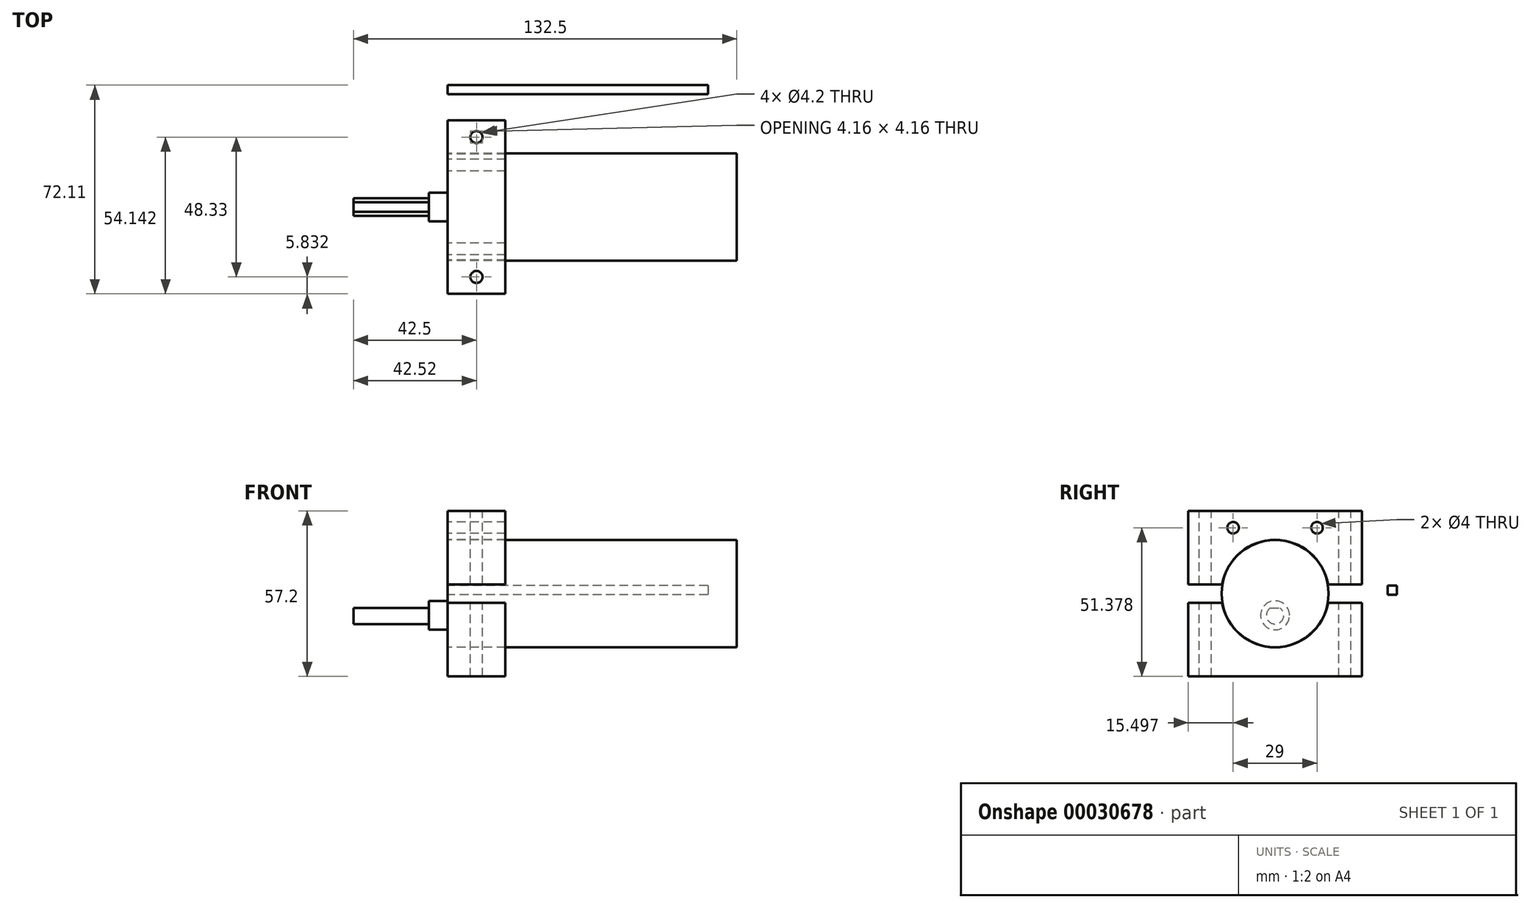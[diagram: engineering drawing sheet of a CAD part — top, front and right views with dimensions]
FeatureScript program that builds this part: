
annotation { "Feature Type Name" : "Feature", "Feature Type Description" : "" }
export const myFeature = defineFeature(function(context is Context, id is Id, definition is map)
    precondition{}
    {
        {
            var Q0;
            Q0=qCreatedBy(makeId("Right.planeOp"),FACE);
            var sketch = newSketch(context, id + "F0", { "sketchPlane" : qUnion([Q0])});
            skLineSegment(sketch, "E0", {"start": v(-30.1, 27.66) * mm, "end": v(29.9, 27.66) * mm});
            skLineSegment(sketch, "E1", {"start": v(-30.1, 27.66) * mm, "end": v(-30.1, 2.22) * mm});
            skLineSegment(sketch, "E2", {"start": v(29.9, 27.66) * mm, "end": v(29.9, 2.22) * mm});
            skPoint(sketch, "E3", {"position": v(-0.1, -0.94) * mm});
            skArc(sketch, "E4", {"start": v(18.23, 2.22) * mm, "mid": v(-0.1, 17.66) * mm, "end": v(-18.43, 2.22) * mm});
            skPoint(sketch, "E5", {"position": v(-0.1, 17.66) * mm});
            skLineSegment(sketch, "E6.trimOffspring", {"start": v(18.23, 2.22) * mm, "end": v(29.9, 2.22) * mm});
            skPoint(sketch, "E7.start.orphan", {"position": v(-0.1, 27.66) * mm});
            skLineSegment(sketch, "E8", {"start": v(-30.1, 2.22) * mm, "end": v(-18.43, 2.22) * mm});
            skCircle(sketch, "E9", {"center": v(-0.1, -0.94) * mm, "radius": 18.5 * mm});
            skLineSegment(sketch, "E10", {"start": v(-30.1, -0.94) * mm, "end": v(34.22, -0.94) * mm});
            skLineSegment(sketch, "E11.MirrorCS", {"start": v(29.9, -29.54) * mm, "end": v(29.9, -4.1) * mm});
            skLineSegment(sketch, "E12.MirrorCS", {"start": v(18.23, -4.1) * mm, "end": v(29.9, -4.1) * mm});
            skLineSegment(sketch, "E13.MirrorCS", {"start": v(-30.1, -29.54) * mm, "end": v(29.9, -29.54) * mm});
            skLineSegment(sketch, "E14.MirrorCS", {"start": v(-30.1, -29.54) * mm, "end": v(-30.1, -4.1) * mm});
            skLineSegment(sketch, "E15.MirrorCS", {"start": v(-30.1, -4.1) * mm, "end": v(-18.43, -4.1) * mm});
            skArc(sketch, "E16.MirrorCS", {"start": v(18.23, -4.1) * mm, "mid": v(-0.1, -19.54) * mm, "end": v(-18.43, -4.1) * mm});
            skCircle(sketch, "E17", {"center": v(-0.1, -0.94) * mm, "radius": 12.5 * mm});
            skPoint(sketch, "E18", {"position": v(-0.1, -8.44) * mm});
            skPoint(sketch, "E19.end.orphan", {"position": v(-0.1, -13.44) * mm});
            skCircle(sketch, "E20", {"center": v(-0.1, -8.44) * mm, "radius": 5 * mm});
            skSolve(sketch);
        }
        {
            var Q0;
            Q0=makeQuery(id+"F0.imprint","IMPRINT",FACE,{"disambiguationData":[TD([[makeQuery(id+"F0.imprint","IMPRINT",EDGE,{"derivedFrom":sQuery(id+"F0.wireOp",EDGE,"E0")}),-1.0]])]});
            var Q1;
            Q1=makeQuery(id+"F0.imprint","IMPRINT",FACE,{"disambiguationData":[TD([[makeQuery(id+"F0.imprint","IMPRINT",EDGE,{"derivedFrom":sQuery(id+"F0.wireOp",EDGE,"E11.MirrorCS")}),1.0]])]});
            extrude(context, id + "F1", {"entities" : qUnion([Q0, Q1]), "depth" : 20 * mm});
        }
        {
            var Q0;
            Q0=makeQuery(id+"F1.opExtrude","SWEPT_FACE",FACE,{"disambiguationData":[OSD([sQuery(id+"F0.wireOp",EDGE,"E0")])]});
            var sketch = newSketch(context, id + "F2", { "sketchPlane" : qUnion([Q0])});
            skPoint(sketch, "E21.0", {"position": v(0, -30.1) * mm});
            skPoint(sketch, "E22.0", {"position": v(20, -30.1) * mm});
            skPoint(sketch, "E23.0", {"position": v(0, 29.9) * mm});
            skPoint(sketch, "E24.0", {"position": v(20, 29.9) * mm});
            skLineSegment(sketch, "E25.0.0", {"start": v(0, 29.9) * mm, "end": v(0, -30.1) * mm});
            skLineSegment(sketch, "E25.0.1", {"start": v(0, -30.1) * mm, "end": v(20, -30.1) * mm});
            skLineSegment(sketch, "E25.0.2", {"start": v(20, -30.1) * mm, "end": v(20, 29.9) * mm});
            skLineSegment(sketch, "E25.0.3", {"start": v(20, 29.9) * mm, "end": v(0, 29.9) * mm});
            skPoint(sketch, "E26.0", {"position": v(0, -18.43) * mm});
            skPoint(sketch, "E27.0", {"position": v(20, -18.43) * mm});
            skPoint(sketch, "E28.0", {"position": v(20, 18.23) * mm});
            skPoint(sketch, "E29.0", {"position": v(0, 18.23) * mm});
            skCircle(sketch, "E30", {"center": v(10, 24.06) * mm, "radius": 2.1 * mm});
            skCircle(sketch, "E31", {"center": v(10, -24.27) * mm, "radius": 2.1 * mm});
            skSolve(sketch);
        }
        {
            var Q0;
            Q0=makeQuery(id+"F2.imprint","IMPRINT",FACE,{"disambiguationData":[TD([[makeQuery(id+"F2.imprint","IMPRINT",EDGE,{"derivedFrom":sQuery(id+"F2.wireOp",EDGE,"E31")}),1.0]])]});
            var Q1;
            Q1=makeQuery(id+"F2.imprint","IMPRINT",FACE,{"disambiguationData":[TD([[makeQuery(id+"F2.imprint","IMPRINT",EDGE,{"derivedFrom":sQuery(id+"F2.wireOp",EDGE,"E30")}),1.0]])]});
            var Q2;
            Q2=makeQuery(id+"F1.opExtrude","SWEPT_FACE",FACE,{"disambiguationData":[OSD([sQuery(id+"F0.wireOp",EDGE,"E13.MirrorCS")])]});
            extrude(context, id + "F3", {"entities" : qUnion([Q0, Q1]), "operationType" : NewBodyOperationType.REMOVE, "endBound" : BoundingType.UP_TO_SURFACE, "oppositeDirection" : true, "endBoundEntityFace" : qUnion([Q2]), "depth" : 25 * mm});
        }
        {
            var Q0;
            Q0=qCreatedBy(makeId("Right.planeOp"),FACE);
            var sketch = newSketch(context, id + "F4", { "sketchPlane" : qUnion([Q0])});
            skLineSegment(sketch, "E32.bottom", {"start": v(42.01, 1.83) * mm, "end": v(38.84, 1.83) * mm});
            skLineSegment(sketch, "E32.top", {"start": v(42.01, -1.34) * mm, "end": v(38.84, -1.34) * mm});
            skLineSegment(sketch, "E32.left", {"start": v(42.01, 1.83) * mm, "end": v(42.01, -1.34) * mm});
            skLineSegment(sketch, "E32.right", {"start": v(38.84, 1.83) * mm, "end": v(38.84, -1.34) * mm});
            skPoint(sketch, "E33", {"position": v(40.43, 0.25) * mm});
            skSolve(sketch);
        }
        {
            var Q0;
            Q0=makeQuery(id+"F4.imprint","IMPRINT",FACE,{"disambiguationData":[TD([[makeQuery(id+"F4.imprint","IMPRINT",EDGE,{"derivedFrom":sQuery(id+"F4.wireOp",EDGE,"E32.bottom")}),1.0]])]});
            extrude(context, id + "F5", {"entities" : qUnion([Q0]), "depth" : 90 * mm});
        }
        {
            var Q0;
            {var subQ2=sQuery(id+"F0.wireOp",EDGE,"E10");var subQ4=sQuery(id+"F0.wireOp",EDGE,"E9");var subQ5=makeQuery(id+"F0.imprint","INTERSECT",VERTEX,{"disambiguationData":[OD(0.0)],"derivedFrom":[subQ4,subQ2]});Q0=makeQuery(id+"F0.imprint","IMPRINT",FACE,{"disambiguationData":[TD([[makeQuery(id+"F0.imprint","IMPRINT",EDGE,{"disambiguationData":[TD([[subQ5,-1.0]])],"derivedFrom":subQ4}),1.0]])]});}
            var Q1;
            {var subQ4=sQuery(id+"F0.wireOp",EDGE,"E20");Q1=makeQuery(id+"F0.imprint","IMPRINT",FACE,{"disambiguationData":[TD([[makeQuery(id+"F0.imprint","IMPRINT",EDGE,{"derivedFrom":subQ4}),-1.0]])]});}
            var Q2;
            {var subQ0=sQuery(id+"F0.wireOp",EDGE,"E10");var subQ1=sQuery(id+"F0.wireOp",EDGE,"E9");var subQ2=makeQuery(id+"F0.imprint","INTERSECT",VERTEX,{"disambiguationData":[OD(0.0)],"derivedFrom":[subQ1,subQ0]});Q2=makeQuery(id+"F0.imprint","IMPRINT",FACE,{"disambiguationData":[TD([[makeQuery(id+"F0.imprint","IMPRINT",EDGE,{"disambiguationData":[TD([[subQ2,1.0]])],"derivedFrom":subQ1}),1.0]])]});}
            var Q3;
            {var subQ0=sQuery(id+"F0.wireOp",EDGE,"E17");var subQ1=sQuery(id+"F0.wireOp",EDGE,"E10");var subQ2=makeQuery(id+"F0.imprint","INTERSECT",VERTEX,{"disambiguationData":[OD(0.0)],"derivedFrom":[subQ1,subQ0]});Q3=makeQuery(id+"F0.imprint","IMPRINT",FACE,{"disambiguationData":[TD([[makeQuery(id+"F0.imprint","IMPRINT",EDGE,{"disambiguationData":[TD([[subQ2,-1.0]])],"derivedFrom":subQ1}),1.0]])]});}
            var Q4;
            Q4=makeQuery(id+"F0.imprint","IMPRINT",FACE,{"disambiguationData":[TD([[makeQuery(id+"F0.imprint","IMPRINT",EDGE,{"derivedFrom":sQuery(id+"F0.wireOp",EDGE,"E20")}),1.0]])]});
            extrude(context, id + "F6", {"entities" : qUnion([Q0, Q1, Q2, Q3, Q4]), "depth" : 100 * mm});
        }
        {
            var Q0;
            Q0=makeQuery(id+"F0.imprint","IMPRINT",FACE,{"disambiguationData":[TD([[makeQuery(id+"F0.imprint","IMPRINT",EDGE,{"derivedFrom":sQuery(id+"F0.wireOp",EDGE,"E20")}),1.0]])]});
            extrude(context, id + "F7", {"entities" : qUnion([Q0]), "operationType" : NewBodyOperationType.ADD, "oppositeDirection" : true, "depth" : 6.5 * mm});
        }
        {
            var Q0;
            Q0=qCreatedBy(makeId("Right.planeOp"),FACE);
            var sketch = newSketch(context, id + "F8", { "sketchPlane" : qUnion([Q0])});
            skPoint(sketch, "E34.0", {"position": v(-0.1, 17.66) * mm});
            skPoint(sketch, "E35.0", {"position": v(-0.1, 27.66) * mm});
            skCircle(sketch, "E36.0", {"center": v(-0.1, -0.94) * mm, "radius": 12.5 * mm, "construction": true});
            skLineSegment(sketch, "E37", {"start": v(-0.1, 17.66) * mm, "end": v(-0.1, 11.56) * mm, "construction": true});
            skCircle(sketch, "E38.0", {"center": v(-0.1, -0.94) * mm, "radius": 18.5 * mm, "construction": true});
            skArc(sketch, "E38.1", {"start": v(18.23, 2.22) * mm, "mid": v(-0.1, 17.66) * mm, "end": v(-18.43, 2.22) * mm, "construction": true});
            skLineSegment(sketch, "E39", {"start": v(-0.1, 27.66) * mm, "end": v(14.4, 21.84) * mm, "construction": true});
            skLineSegment(sketch, "E40", {"start": v(-0.1, 27.66) * mm, "end": v(-14.6, 21.84) * mm, "construction": true});
            skLineSegment(sketch, "E41", {"start": v(-14.6, 21.84) * mm, "end": v(14.4, 21.84) * mm, "construction": true});
            skCircle(sketch, "E42", {"center": v(14.4, 21.84) * mm, "radius": 2 * mm});
            skCircle(sketch, "E43", {"center": v(-14.6, 21.84) * mm, "radius": 2 * mm});
            skLineSegment(sketch, "E44.0", {"start": v(-30.13, -0.94) * mm, "end": v(29.92, -0.94) * mm, "construction": true});
            skCircle(sketch, "E45.MirrorC", {"center": v(14.4, -23.71) * mm, "radius": 2 * mm});
            skCircle(sketch, "E46.MirrorC", {"center": v(-14.6, -23.71) * mm, "radius": 2 * mm});
            skLineSegment(sketch, "E47", {"start": v(-0.1, 17.66) * mm, "end": v(-0.1, 2.22) * mm, "construction": true});
            skLineSegment(sketch, "E48", {"start": v(14.4, 21.84) * mm, "end": v(-0.1, -0.94) * mm, "construction": true});
            skLineSegment(sketch, "E49", {"start": v(-14.6, 21.84) * mm, "end": v(-0.1, -0.94) * mm, "construction": true});
            skSolve(sketch);
        }
        {
            var Q0;
            Q0=makeQuery(id+"F8.imprint","IMPRINT",FACE,{"disambiguationData":[TD([[makeQuery(id+"F8.imprint","IMPRINT",EDGE,{"derivedFrom":sQuery(id+"F8.wireOp",EDGE,"E45.MirrorC")}),-1.0]])]});
            var Q1;
            Q1=makeQuery(id+"F8.imprint","IMPRINT",FACE,{"disambiguationData":[TD([[makeQuery(id+"F8.imprint","IMPRINT",EDGE,{"derivedFrom":sQuery(id+"F8.wireOp",EDGE,"E46.MirrorC")}),-1.0]])]});
            var Q2;
            Q2=makeQuery(id+"F8.imprint","IMPRINT",FACE,{"disambiguationData":[TD([[makeQuery(id+"F8.imprint","IMPRINT",EDGE,{"derivedFrom":sQuery(id+"F8.wireOp",EDGE,"E42")}),1.0]])]});
            var Q3;
            Q3=makeQuery(id+"F8.imprint","IMPRINT",FACE,{"disambiguationData":[TD([[makeQuery(id+"F8.imprint","IMPRINT",EDGE,{"derivedFrom":sQuery(id+"F8.wireOp",EDGE,"E43")}),1.0]])]});
            var Q4;
            Q4=makeQuery(id+"F1.opExtrude","CAP_FACE",FACE,{"disambiguationData":[OSD([sQuery(id+"F0.wireOp",EDGE,"E0"),sQuery(id+"F0.wireOp",EDGE,"E1"),sQuery(id+"F0.wireOp",EDGE,"E2"),sQuery(id+"F0.wireOp",EDGE,"E4"),sQuery(id+"F0.wireOp",EDGE,"E6.trimOffspring"),sQuery(id+"F0.wireOp",EDGE,"E8")])],"isStart":false});
            extrude(context, id + "F9", {"entities" : qUnion([Q0, Q1, Q2, Q3]), "operationType" : NewBodyOperationType.REMOVE, "endBound" : BoundingType.UP_TO_SURFACE, "endBoundEntityFace" : qUnion([Q4]), "depth" : 25 * mm});
        }
        {
            var Q0;
            Q0=makeQuery(id+"F7.opExtrude","CAP_FACE",FACE,{"disambiguationData":[OSD([sQuery(id+"F0.wireOp",EDGE,"E20")])],"isStart":false});
            var sketch = newSketch(context, id + "F10", { "sketchPlane" : qUnion([Q0])});
            skPoint(sketch, "E50.0", {"position": v(0.1, -8.44) * mm});
            skArc(sketch, "E51", {"start": v(-1.56, -5.94) * mm, "mid": v(0.1, -11.44) * mm, "end": v(1.76, -5.94) * mm});
            skLineSegment(sketch, "E52", {"start": v(0.1, -5.94) * mm, "end": v(1.76, -5.94) * mm});
            skLineSegment(sketch, "E53", {"start": v(0.1, -5.94) * mm, "end": v(-1.56, -5.94) * mm});
            skCircle(sketch, "E54.0", {"center": v(0.1, -8.44) * mm, "radius": 5 * mm, "construction": true});
            skSolve(sketch);
        }
        {
            var Q0;
            Q0=makeQuery(id+"F10.imprint","IMPRINT",FACE,{"disambiguationData":[TD([[makeQuery(id+"F10.imprint","IMPRINT",EDGE,{"derivedFrom":sQuery(id+"F10.wireOp",EDGE,"E51")}),1.0]])]});
            extrude(context, id + "F11", {"entities" : qUnion([Q0]), "operationType" : NewBodyOperationType.ADD, "depth" : 26 * mm});
        }
    });
